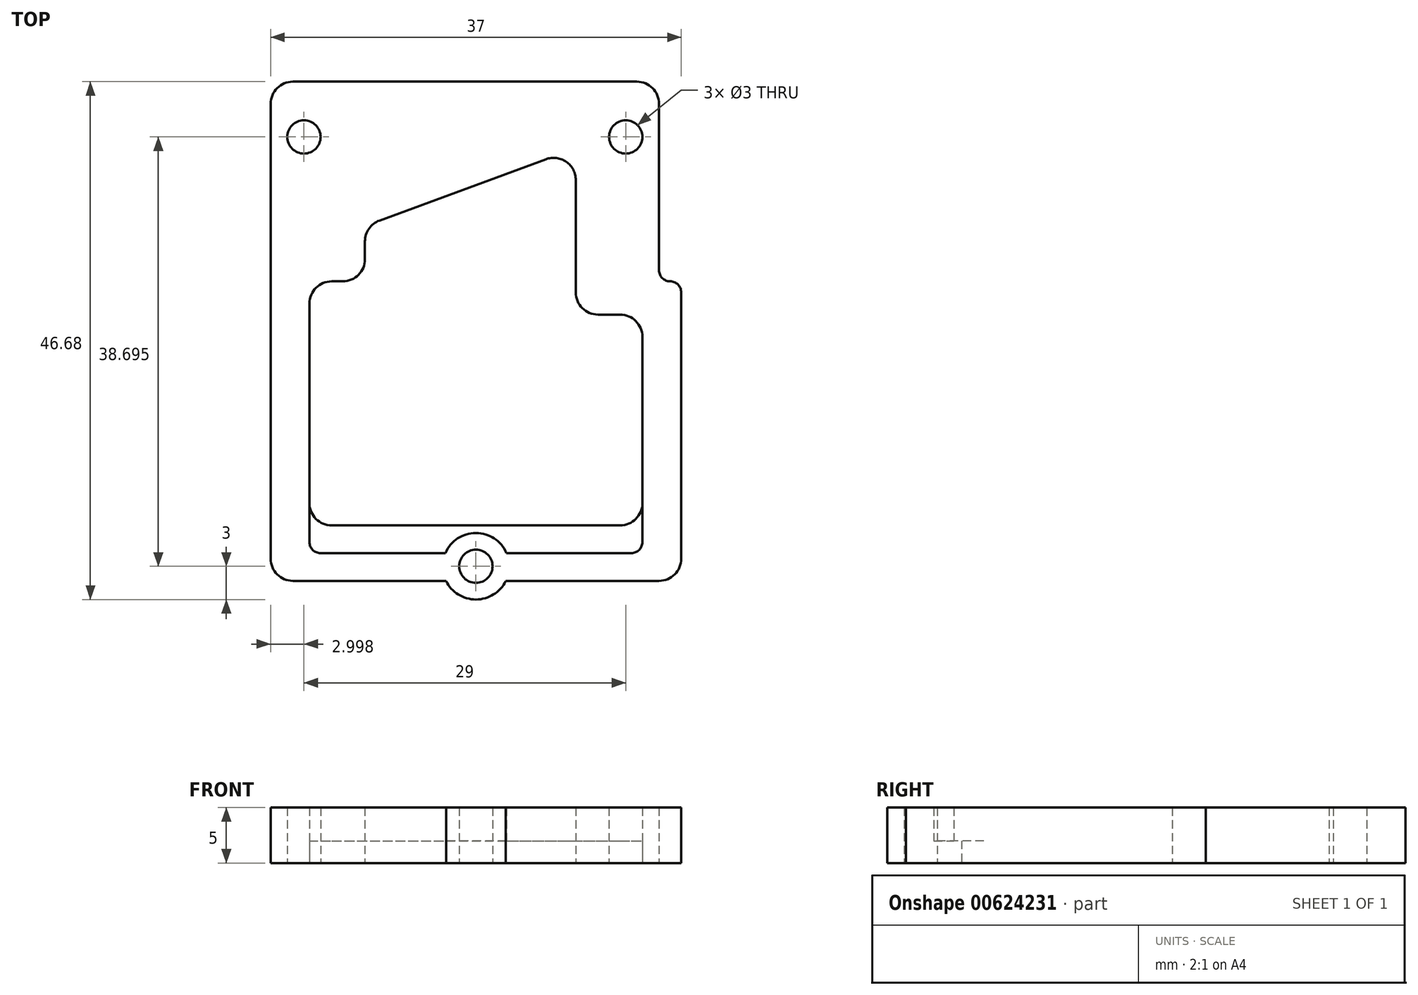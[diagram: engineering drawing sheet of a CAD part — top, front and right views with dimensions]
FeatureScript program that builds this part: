
annotation { "Feature Type Name" : "Feature", "Feature Type Description" : "" }
export const myFeature = defineFeature(function(context is Context, id is Id, definition is map)
    precondition{}
    {
        {
            var Q0;
            Q0=qCreatedBy(makeId("Top.planeOp"),FACE);
            var sketch = newSketch(context, id + "F0", { "sketchPlane" : qUnion([Q0])});
            skLineSegment(sketch, "E0.bottom", {"start": v(-8, 18) * mm, "end": v(23, 18) * mm});
            skLineSegment(sketch, "E0.top", {"start": v(-8, -27) * mm, "end": v(25, -27) * mm});
            skLineSegment(sketch, "E0.left", {"start": v(-10, 16) * mm, "end": v(-10, -25) * mm});
            skLineSegment(sketch, "E0.right", {"start": v(27, -1) * mm, "end": v(27, -25) * mm});
            skLineSegment(sketch, "E1", {"start": v(-4.5, -22) * mm, "end": v(21.5, -22) * mm});
            skLineSegment(sketch, "E2", {"start": v(23.5, -20) * mm, "end": v(23.5, -5) * mm});
            skLineSegment(sketch, "E3", {"start": v(21.5, -3) * mm, "end": v(19.5, -3) * mm});
            skLineSegment(sketch, "E4", {"start": v(17.5, -1) * mm, "end": v(17.5, 9.13) * mm});
            skLineSegment(sketch, "E5", {"start": v(-6.5, -20) * mm, "end": v(-6.5, -2) * mm});
            skLineSegment(sketch, "E6", {"start": v(-4.5, 0) * mm, "end": v(-3.5, 0) * mm});
            skLineSegment(sketch, "E7", {"start": v(-1.5, 2) * mm, "end": v(-1.5, 3.6) * mm});
            skLineSegment(sketch, "E8", {"start": v(-0.18, 5.48) * mm, "end": v(14.82, 11) * mm});
            skLineSegment(sketch, "E9", {"start": v(25, 16) * mm, "end": v(25, 1) * mm});
            skLineSegment(sketch, "E10", {"start": v(26, 0) * mm, "end": v(26, 0) * mm});
            skPoint(sketch, "E11.visualSharp", {"position": v(-6.5, -22) * mm});
            skArc(sketch, "E11.filletArc", {"start": v(-6.5, -20) * mm, "mid": v(-5.9, -21.41) * mm, "end": v(-4.5, -22) * mm});
            skPoint(sketch, "E12.visualSharp", {"position": v(-6.5, 0) * mm});
            skArc(sketch, "E12.filletArc", {"start": v(-4.5, 0) * mm, "mid": v(-5.9, -0.59) * mm, "end": v(-6.5, -2) * mm});
            skPoint(sketch, "E13.visualSharp", {"position": v(-1.5, 5) * mm});
            skArc(sketch, "E13.filletArc", {"start": v(-0.18, 5.48) * mm, "mid": v(-1.13, 4.75) * mm, "end": v(-1.5, 3.6) * mm});
            skPoint(sketch, "E14.visualSharp", {"position": v(-1.5, 0) * mm});
            skArc(sketch, "E14.filletArc", {"start": v(-3.5, 0) * mm, "mid": v(-2.08, 0.59) * mm, "end": v(-1.5, 2) * mm});
            skPoint(sketch, "E15.visualSharp", {"position": v(17.5, 12) * mm});
            skArc(sketch, "E15.filletArc", {"start": v(17.5, 9.13) * mm, "mid": v(16.65, 10.77) * mm, "end": v(14.82, 11) * mm});
            skPoint(sketch, "E16.visualSharp", {"position": v(23.5, -22) * mm});
            skArc(sketch, "E16.filletArc", {"start": v(21.5, -22) * mm, "mid": v(22.92, -21.41) * mm, "end": v(23.5, -20) * mm});
            skPoint(sketch, "E17.visualSharp", {"position": v(-10, -27) * mm});
            skArc(sketch, "E17.filletArc", {"start": v(-10, -25) * mm, "mid": v(-9.4, -26.41) * mm, "end": v(-8, -27) * mm});
            skPoint(sketch, "E18.visualSharp", {"position": v(27, -27) * mm});
            skArc(sketch, "E18.filletArc", {"start": v(25, -27) * mm, "mid": v(26.42, -26.41) * mm, "end": v(27, -25) * mm});
            skPoint(sketch, "E19.visualSharp", {"position": v(25, 18) * mm});
            skArc(sketch, "E19.filletArc", {"start": v(25, 16) * mm, "mid": v(24.42, 17.41) * mm, "end": v(23, 18) * mm});
            skPoint(sketch, "E20.visualSharp", {"position": v(-10, 18) * mm});
            skArc(sketch, "E20.filletArc", {"start": v(-8, 18) * mm, "mid": v(-9.4, 17.41) * mm, "end": v(-10, 16) * mm});
            skPoint(sketch, "E21.visualSharp", {"position": v(17.5, -3) * mm});
            skArc(sketch, "E21.filletArc", {"start": v(17.5, -1) * mm, "mid": v(18.1, -2.41) * mm, "end": v(19.5, -3) * mm});
            skPoint(sketch, "E22.visualSharp", {"position": v(23.5, -3) * mm});
            skArc(sketch, "E22.filletArc", {"start": v(23.5, -5) * mm, "mid": v(22.92, -3.59) * mm, "end": v(21.5, -3) * mm});
            skPoint(sketch, "E23.visualSharp", {"position": v(25, 0) * mm});
            skArc(sketch, "E23.filletArc", {"start": v(25, 1) * mm, "mid": v(25.3, 0.3) * mm, "end": v(26, 0) * mm});
            skPoint(sketch, "E24.visualSharp", {"position": v(27, 0) * mm});
            skArc(sketch, "E24.filletArc", {"start": v(27, -1) * mm, "mid": v(26.72, -0.3) * mm, "end": v(26, 0) * mm});
            skLineSegment(sketch, "E25", {"start": v(-5.5, -24.5) * mm, "end": v(22.5, -24.5) * mm});
            skLineSegment(sketch, "E26", {"start": v(-6.5, -20) * mm, "end": v(-6.5, -23.5) * mm});
            skLineSegment(sketch, "E27", {"start": v(23.5, -20) * mm, "end": v(23.5, -23.5) * mm});
            skPoint(sketch, "E28.visualSharp", {"position": v(-6.5, -24.5) * mm});
            skArc(sketch, "E28.filletArc", {"start": v(-6.5, -23.5) * mm, "mid": v(-6.2, -24.2) * mm, "end": v(-5.5, -24.5) * mm});
            skPoint(sketch, "E29.visualSharp", {"position": v(23.5, -24.5) * mm});
            skArc(sketch, "E29.filletArc", {"start": v(22.5, -24.5) * mm, "mid": v(23.22, -24.2) * mm, "end": v(23.5, -23.5) * mm});
            skLineSegment(sketch, "E30", {"start": v(8.5, -22) * mm, "end": v(8.5, -27) * mm, "construction": true});
            skCircle(sketch, "E31", {"center": v(8.5, -25.68) * mm, "radius": 1.5 * mm});
            skCircle(sketch, "E32", {"center": v(8.5, -25.68) * mm, "radius": 3 * mm});
            skCircle(sketch, "E33", {"center": v(-7, 13.02) * mm, "radius": 3 * mm});
            skCircle(sketch, "E34", {"center": v(-7, 13.02) * mm, "radius": 1.5 * mm});
            skLineSegment(sketch, "E35", {"start": v(-7, 13.02) * mm, "end": v(22, 13.02) * mm, "construction": true});
            skCircle(sketch, "E36", {"center": v(22, 13.02) * mm, "radius": 3 * mm});
            skCircle(sketch, "E37", {"center": v(22, 13.02) * mm, "radius": 1.5 * mm});
            skSolve(sketch);
        }
        {
            var Q0;
            Q0=makeQuery(id+"F0.imprint","IMPRINT",FACE,{"disambiguationData":[TD([[makeQuery(id+"F0.imprint","IMPRINT",EDGE,{"derivedFrom":sQuery(id+"F0.wireOp",EDGE,"E1")}),-1.0]])]});
            extrude(context, id + "F1", {"entities" : qUnion([Q0]), "depth" : 2 * mm, "offsetDistance" : 25 * mm});
        }
        {
            var Q0;
            Q0 = qSketchRegion(id + "F0", true);
            extrude(context, id + "F2", {"entities" : qUnion([Q0]), "operationType" : NewBodyOperationType.ADD, "depth" : 5 * mm, "offsetDistance" : 25 * mm});
        }
        {
            var Q0;
            {var subQ0=sQuery(id+"F0.wireOp",EDGE,"E32");var subQ1=sQuery(id+"F0.wireOp",EDGE,"E25");var subQ2=makeQuery(id+"F0.imprint","INTERSECT",VERTEX,{"disambiguationData":[OD(0.0)],"derivedFrom":[subQ1,subQ0]});Q0=makeQuery(id+"F0.imprint","IMPRINT",FACE,{"disambiguationData":[TD([[makeQuery(id+"F0.imprint","IMPRINT",EDGE,{"disambiguationData":[TD([[subQ2,-1.0]])],"derivedFrom":subQ1}),1.0]])]});}
            extrude(context, id + "F3", {"entities" : qUnion([Q0]), "operationType" : NewBodyOperationType.ADD, "depth" : 5 * mm, "offsetDistance" : 25 * mm});
        }
    });
